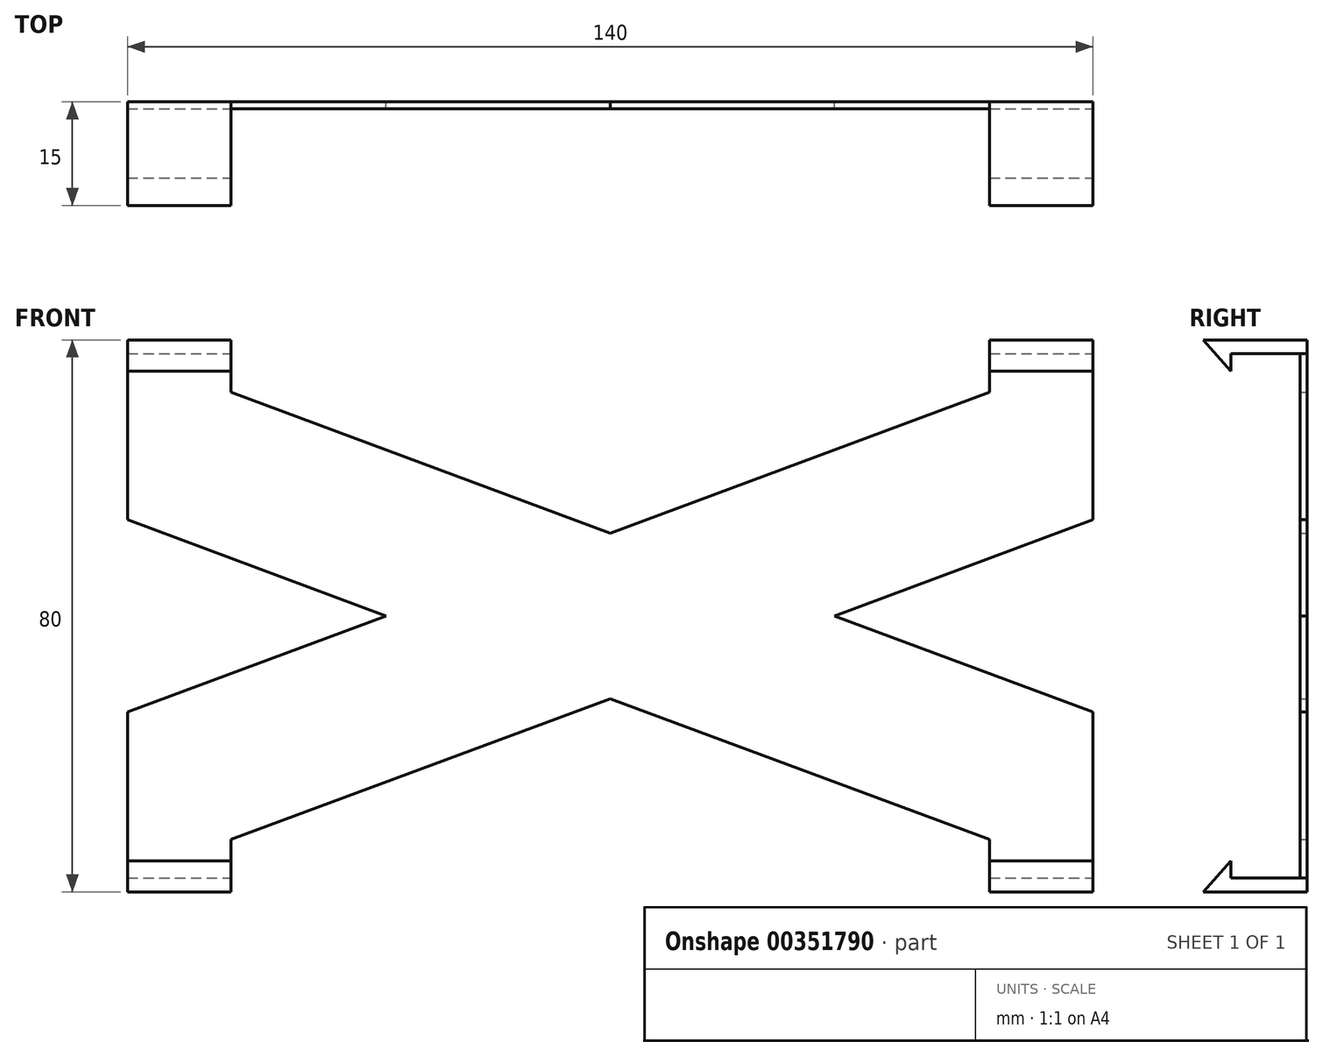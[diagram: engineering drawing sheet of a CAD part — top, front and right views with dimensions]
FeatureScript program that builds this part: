
annotation { "Feature Type Name" : "Feature", "Feature Type Description" : "" }
export const myFeature = defineFeature(function(context is Context, id is Id, definition is map)
    precondition{}
    {
        {
            var Q0;
            Q0=qCreatedBy(makeId("Front.planeOp"),FACE);
            var sketch = newSketch(context, id + "F0", { "sketchPlane" : qUnion([Q0])});
            skLineSegment(sketch, "E0.bottom", {"start": v(-70, 38) * mm, "end": v(-55, 38) * mm});
            skLineSegment(sketch, "E0.top", {"start": v(-70, -38) * mm, "end": v(-55, -38) * mm});
            skLineSegment(sketch, "E0.left", {"start": v(-70, 38) * mm, "end": v(-70, 13.93) * mm});
            skLineSegment(sketch, "E0.right", {"start": v(70, 38) * mm, "end": v(70, 13.93) * mm});
            skPoint(sketch, "E0.middle", {"position": v(0, 0) * mm});
            skLineSegment(sketch, "E1", {"start": v(0, 12) * mm, "end": v(-55, 32.43) * mm});
            skLineSegment(sketch, "E2", {"start": v(0, -12) * mm, "end": v(-55, -32.43) * mm});
            skLineSegment(sketch, "E3", {"start": v(-70, 13.93) * mm, "end": v(-32.5, 0) * mm});
            skLineSegment(sketch, "E4", {"start": v(-32.5, 0) * mm, "end": v(-70, -13.93) * mm});
            skLineSegment(sketch, "E5.trimOffspring", {"start": v(-70, -13.93) * mm, "end": v(-70, -38) * mm});
            skLineSegment(sketch, "E6", {"start": v(0, 12) * mm, "end": v(55, 32.43) * mm});
            skLineSegment(sketch, "E7", {"start": v(0, -12) * mm, "end": v(55, -32.43) * mm});
            skLineSegment(sketch, "E8", {"start": v(32.5, 0) * mm, "end": v(70, 13.93) * mm});
            skLineSegment(sketch, "E9", {"start": v(32.5, 0) * mm, "end": v(70, -13.93) * mm});
            skLineSegment(sketch, "E10.trimOffspring", {"start": v(70, -13.93) * mm, "end": v(70, -38) * mm});
            skLineSegment(sketch, "E11", {"start": v(-55, 32.43) * mm, "end": v(-55, 38) * mm});
            skLineSegment(sketch, "E12", {"start": v(55, 32.43) * mm, "end": v(55, 38) * mm});
            skLineSegment(sketch, "E13", {"start": v(-55, -32.43) * mm, "end": v(-55, -38) * mm});
            skLineSegment(sketch, "E14", {"start": v(55, -32.43) * mm, "end": v(55, -38) * mm});
            skLineSegment(sketch, "E15.trimOffspring", {"start": v(55, 38) * mm, "end": v(70, 38) * mm});
            skLineSegment(sketch, "E16.trimOffspring", {"start": v(55, -38) * mm, "end": v(70, -38) * mm});
            skLineSegment(sketch, "E17.top", {"start": v(-70, 40) * mm, "end": v(-55, 40) * mm});
            skLineSegment(sketch, "E17.left", {"start": v(-70, 38) * mm, "end": v(-70, 40) * mm});
            skLineSegment(sketch, "E17.right", {"start": v(-55, 38) * mm, "end": v(-55, 40) * mm});
            skLineSegment(sketch, "E18.top", {"start": v(55, 40) * mm, "end": v(70, 40) * mm});
            skLineSegment(sketch, "E18.left", {"start": v(55, 38) * mm, "end": v(55, 40) * mm});
            skLineSegment(sketch, "E18.right", {"start": v(70, 38) * mm, "end": v(70, 40) * mm});
            skLineSegment(sketch, "E19.top", {"start": v(-70, -40) * mm, "end": v(-55, -40) * mm});
            skLineSegment(sketch, "E19.left", {"start": v(-70, -38) * mm, "end": v(-70, -40) * mm});
            skLineSegment(sketch, "E19.right", {"start": v(-55, -38) * mm, "end": v(-55, -40) * mm});
            skLineSegment(sketch, "E20.top", {"start": v(55, -40) * mm, "end": v(70, -40) * mm});
            skLineSegment(sketch, "E20.left", {"start": v(55, -38) * mm, "end": v(55, -40) * mm});
            skLineSegment(sketch, "E20.right", {"start": v(70, -38) * mm, "end": v(70, -40) * mm});
            skSolve(sketch);
        }
        {
            var Q0;
            Q0=makeQuery(id+"F0.imprint","IMPRINT",FACE,{"disambiguationData":[TD([[makeQuery(id+"F0.imprint","IMPRINT",EDGE,{"derivedFrom":sQuery(id+"F0.wireOp",EDGE,"E0.bottom")}),-1.0]])]});
            extrude(context, id + "F1", {"entities" : qUnion([Q0]), "depth" : 1 * mm});
        }
        {
            var Q0;
            Q0=makeQuery(id+"F0.imprint","IMPRINT",FACE,{"disambiguationData":[TD([[makeQuery(id+"F0.imprint","IMPRINT",EDGE,{"derivedFrom":sQuery(id+"F0.wireOp",EDGE,"E15.trimOffspring")}),1.0]])]});
            var Q1;
            Q1=makeQuery(id+"F0.imprint","IMPRINT",FACE,{"disambiguationData":[TD([[makeQuery(id+"F0.imprint","IMPRINT",EDGE,{"derivedFrom":sQuery(id+"F0.wireOp",EDGE,"E0.bottom")}),1.0]])]});
            var Q2;
            Q2=makeQuery(id+"F0.imprint","IMPRINT",FACE,{"disambiguationData":[TD([[makeQuery(id+"F0.imprint","IMPRINT",EDGE,{"derivedFrom":sQuery(id+"F0.wireOp",EDGE,"E0.top")}),-1.0]])]});
            var Q3;
            Q3=makeQuery(id+"F0.imprint","IMPRINT",FACE,{"disambiguationData":[TD([[makeQuery(id+"F0.imprint","IMPRINT",EDGE,{"derivedFrom":sQuery(id+"F0.wireOp",EDGE,"E16.trimOffspring")}),-1.0]])]});
            extrude(context, id + "F2", {"entities" : qUnion([Q0, Q1, Q2, Q3]), "depth" : 11 * mm});
        }
        {
            var Q0;
            Q0=makeQuery(id+"F0.imprint","IMPRINT",FACE,{"disambiguationData":[TD([[makeQuery(id+"F0.imprint","IMPRINT",EDGE,{"derivedFrom":sQuery(id+"F0.wireOp",EDGE,"E0.left")}),1.0]])]});
            extrude(context, id + "F3", {"entities" : qUnion([Q0]), "depth" : 1 * mm});
        }
        {
            var Q0;
            Q0=makeQuery(id+"F2.opExtrude","SWEPT_FACE",FACE,{"disambiguationData":[OSD([sQuery(id+"F0.wireOp",EDGE,"E18.right")])]});
            var sketch = newSketch(context, id + "F4", { "sketchPlane" : qUnion([Q0])});
            skLineSegment(sketch, "E21", {"start": v(-11, 38) * mm, "end": v(-11, 35.5) * mm});
            skLineSegment(sketch, "E22", {"start": v(-11, 35.5) * mm, "end": v(-15, 40) * mm});
            skLineSegment(sketch, "E23", {"start": v(-15, 40) * mm, "end": v(-11, 40) * mm});
            skLineSegment(sketch, "E24", {"start": v(-11, 38) * mm, "end": v(-11, 40) * mm});
            skSolve(sketch);
        }
        {
            var Q0;
            Q0 = qSketchRegion(id + "F4", true);
            extrude(context, id + "F5", {"entities" : qUnion([Q0]), "operationType" : NewBodyOperationType.ADD, "oppositeDirection" : true, "depth" : 15 * mm});
        }
        {
            var Q0;
            Q0=makeQuery(id+"F2.opExtrude","SWEPT_FACE",FACE,{"disambiguationData":[OSD([sQuery(id+"F0.wireOp",EDGE,"E17.left")])]});
            var sketch = newSketch(context, id + "F6", { "sketchPlane" : qUnion([Q0])});
            skLineSegment(sketch, "E25", {"start": v(11, 40) * mm, "end": v(15, 40) * mm});
            skLineSegment(sketch, "E26", {"start": v(15, 40) * mm, "end": v(11, 35.5) * mm});
            skLineSegment(sketch, "E27", {"start": v(11, 35.5) * mm, "end": v(11, 40) * mm});
            skSolve(sketch);
        }
        {
            var Q0;
            {var subQ0=sQuery(id+"F6.wireOp",EDGE,"E25");Q0=makeQuery(id+"F6.imprint","IMPRINT",FACE,{"disambiguationData":[TD([[makeQuery(id+"F6.imprint","IMPRINT",EDGE,{"derivedFrom":subQ0}),-1.0]])]});}
            extrude(context, id + "F7", {"entities" : qUnion([Q0]), "operationType" : NewBodyOperationType.ADD, "oppositeDirection" : true, "depth" : 15 * mm});
        }
        {
            var Q0;
            Q0=makeQuery(id+"F2.opExtrude","SWEPT_FACE",FACE,{"disambiguationData":[OSD([sQuery(id+"F0.wireOp",EDGE,"E20.right")])]});
            var sketch = newSketch(context, id + "F8", { "sketchPlane" : qUnion([Q0])});
            skLineSegment(sketch, "E28", {"start": v(-11, -40) * mm, "end": v(-15, -40) * mm});
            skLineSegment(sketch, "E29", {"start": v(-15, -40) * mm, "end": v(-11, -35.5) * mm});
            skLineSegment(sketch, "E30", {"start": v(-11, -35.5) * mm, "end": v(-11, -40) * mm});
            skSolve(sketch);
        }
        {
            var Q0;
            Q0 = qSketchRegion(id + "F8", true);
            extrude(context, id + "F9", {"entities" : qUnion([Q0]), "operationType" : NewBodyOperationType.ADD, "oppositeDirection" : true, "depth" : 15 * mm});
        }
        {
            var Q0;
            Q0=makeQuery(id+"F2.opExtrude","SWEPT_FACE",FACE,{"disambiguationData":[OSD([sQuery(id+"F0.wireOp",EDGE,"E19.left")])]});
            var sketch = newSketch(context, id + "F10", { "sketchPlane" : qUnion([Q0])});
            skLineSegment(sketch, "E31", {"start": v(11, -40) * mm, "end": v(15, -40) * mm});
            skLineSegment(sketch, "E32", {"start": v(15, -40) * mm, "end": v(11, -35.5) * mm});
            skLineSegment(sketch, "E33", {"start": v(11, -35.5) * mm, "end": v(11, -40) * mm});
            skSolve(sketch);
        }
        {
            var Q0;
            Q0 = qSketchRegion(id + "F10", true);
            extrude(context, id + "F11", {"entities" : qUnion([Q0]), "operationType" : NewBodyOperationType.ADD, "oppositeDirection" : true, "depth" : 15 * mm});
        }
    });
